# Revit family: Skyfull_Porta-de-Giro-1-Folha-Vidro
name_source: partatom
category: Doors
units: mm (PartAtom-declared; Revit-internal decimal feet)

## family parameters
Always vertical = Yes
Cut with Voids When Loaded = No
Host = Wall
OmniClass Number = 23.30.10.00
OmniClass Title = Doors
Room Calculation Point = No
Shared = No

## types (16) — shared parameters
Altura Maçaneta = 110 cm
Analytic Construction = <Nenhum>
Define Thermal Properties by = Schematic Type
Description = Porta com esquadria minimalista de alumínio e vidro, 1 Folha
Developer = Blocks
Height = 210 cm
Manufacturer = Ulimax&Co
Rough Height = 219.14 cm
Thickness = 5 cm
Type Comments = Porta de Giro Skyfull
URL = https://www.ulimax.com.br
URL Developer = https://BlocksRvt.com
URL Produto = https://www.skyfull.com.br
URL Template = https://www.skyfull.com.br
Visor = Skyfull - Glass - Transparent
Wall Closure = By host

## per-type parameters (varying)
| type | Batente | Caixilho | Puxador | Rough Width | Width |
| Branco - 0.70 x 2.10 | Skyfull - Metal - White - Matte - 246-246-243 | Skyfull - Metal - White - Matte - 246-246-243 | Skyfull - Metal - White - Matte - 246-246-243 | 79.14 cm | 70 cm |
| Cinza - 0.60 x 2.10 | Skyfull - Metal - Chrome - 203-203-203 | Skyfull - Metal - Chrome - 203-203-203 | Skyfull - Metal - Chrome - 203-203-203 | 69.14 cm | 60 cm |
| Cinza - 0.80 x 2.10 | Skyfull - Metal - Chrome - 203-203-203 | Skyfull - Metal - Chrome - 203-203-203 | Skyfull - Metal - Chrome - 203-203-203 | 89.14 cm | 80 cm |
| Branco - 0.90 x 2.10 | Skyfull - Metal - White - Matte - 246-246-243 | Skyfull - Metal - White - Matte - 246-246-243 | Skyfull - Metal - White - Matte - 246-246-243 | 99.14 cm | 90 cm |
| Preto - 0.70 x 2.10 | Skyfull - Metal - Black - Matte - 15-15-15 | Skyfull - Metal - Black - Matte - 15-15-15 | Skyfull - Metal - Black - Matte - 15-15-15 | 79.14 cm | 70 cm |
| Preto - 0.80 x 2.10 | Skyfull - Metal - Black - Matte - 15-15-15 | Skyfull - Metal - Black - Matte - 15-15-15 | Skyfull - Metal - Black - Matte - 15-15-15 | 89.14 cm | 80 cm |
| Preto - 0.90 x 2.10 | Skyfull - Metal - Black - Matte - 15-15-15 | Skyfull - Metal - Black - Matte - 15-15-15 | Skyfull - Metal - Black - Matte - 15-15-15 | 99.14 cm | 90 cm |
| Preto - 0.60 x 2.10 | Skyfull - Metal - Black - Matte - 15-15-15 | Skyfull - Metal - Black - Matte - 15-15-15 | Skyfull - Metal - Black - Matte - 15-15-15 | 69.14 cm | 60 cm |
| Branco - 0.60 x 2.10 | Skyfull - Metal - White - Matte - 246-246-243 | Skyfull - Metal - White - Matte - 246-246-243 | Skyfull - Metal - White - Matte - 246-246-243 | 69.14 cm | 60 cm |
| Cinza - 0.70 x 2.10 | Skyfull - Metal - Chrome - 203-203-203 | Skyfull - Metal - Chrome - 203-203-203 | Skyfull - Metal - Chrome - 203-203-203 | 79.14 cm | 70 cm |
| Branco - 0.80 x 2.10 | Skyfull - Metal - White - Matte - 246-246-243 | Skyfull - Metal - White - Matte - 246-246-243 | Skyfull - Metal - White - Matte - 246-246-243 | 89.14 cm | 80 cm |
| Champanhe - 0.60 x 2.10 | Skyfull - Metal - Beige - Matte - 230-200-160 | Skyfull - Metal - Beige - Matte - 230-200-160 | Skyfull - Metal - Beige - Matte - 230-200-160 | 69.14 cm | 60 cm |
| Champanhe - 0.70 x 2.10 | Skyfull - Metal - Beige - Matte - 230-200-160 | Skyfull - Metal - Beige - Matte - 230-200-160 | Skyfull - Metal - Beige - Matte - 230-200-160 | 79.14 cm | 70 cm |
| Champanhe - 0.80 x 2.10 | Skyfull - Metal - Beige - Matte - 230-200-160 | Skyfull - Metal - Beige - Matte - 230-200-160 | Skyfull - Metal - Beige - Matte - 230-200-160 | 89.14 cm | 80 cm |
| Champanhe - 0.90 x 2.10 | Skyfull - Metal - Beige - Matte - 230-200-160 | Skyfull - Metal - Beige - Matte - 230-200-160 | Skyfull - Metal - Beige - Matte - 230-200-160 | 99.14 cm | 90 cm |
| Cinza - 0.90 x 2.10 | Skyfull - Metal - Chrome - 203-203-203 | Skyfull - Metal - Chrome - 203-203-203 | Skyfull - Metal - Chrome - 203-203-203 | 99.14 cm | 90 cm |
